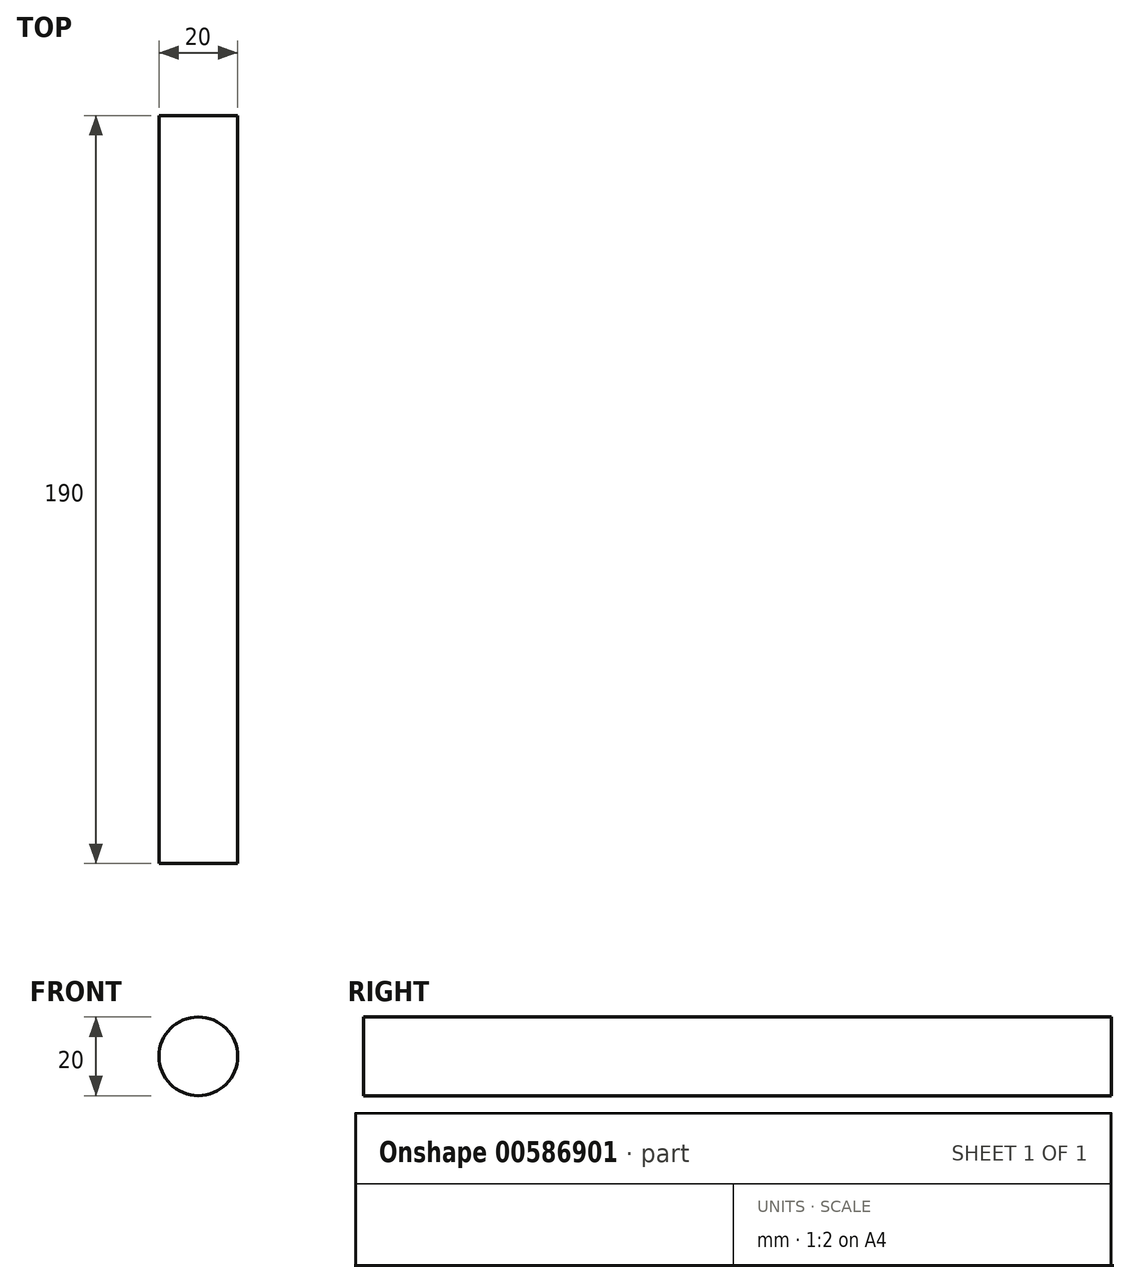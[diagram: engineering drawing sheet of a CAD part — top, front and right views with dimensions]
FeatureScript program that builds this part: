
annotation { "Feature Type Name" : "Feature", "Feature Type Description" : "" }
export const myFeature = defineFeature(function(context is Context, id is Id, definition is map)
    precondition{}
    {
        {
            var Q0;
            Q0=qCreatedBy(makeId("Front.planeOp"),FACE);
            var sketch = newSketch(context, id + "F0", { "sketchPlane" : qUnion([Q0])});
            skCircle(sketch, "E0", {"center": v(0, 0) * mm, "radius": 10 * mm});
            skSolve(sketch);
        }
        {
            var Q0;
            Q0=makeQuery(id+"F0.imprint","IMPRINT",FACE,{"disambiguationData":[TD([[makeQuery(id+"F0.imprint","IMPRINT",EDGE,{"derivedFrom":sQuery(id+"F0.wireOp",EDGE,"E0")}),1.0]])]});
            extrude(context, id + "F1", {"entities" : qUnion([Q0]), "depth" : 190 * mm, "offsetDistance" : 25.4 * mm});
        }
    });
